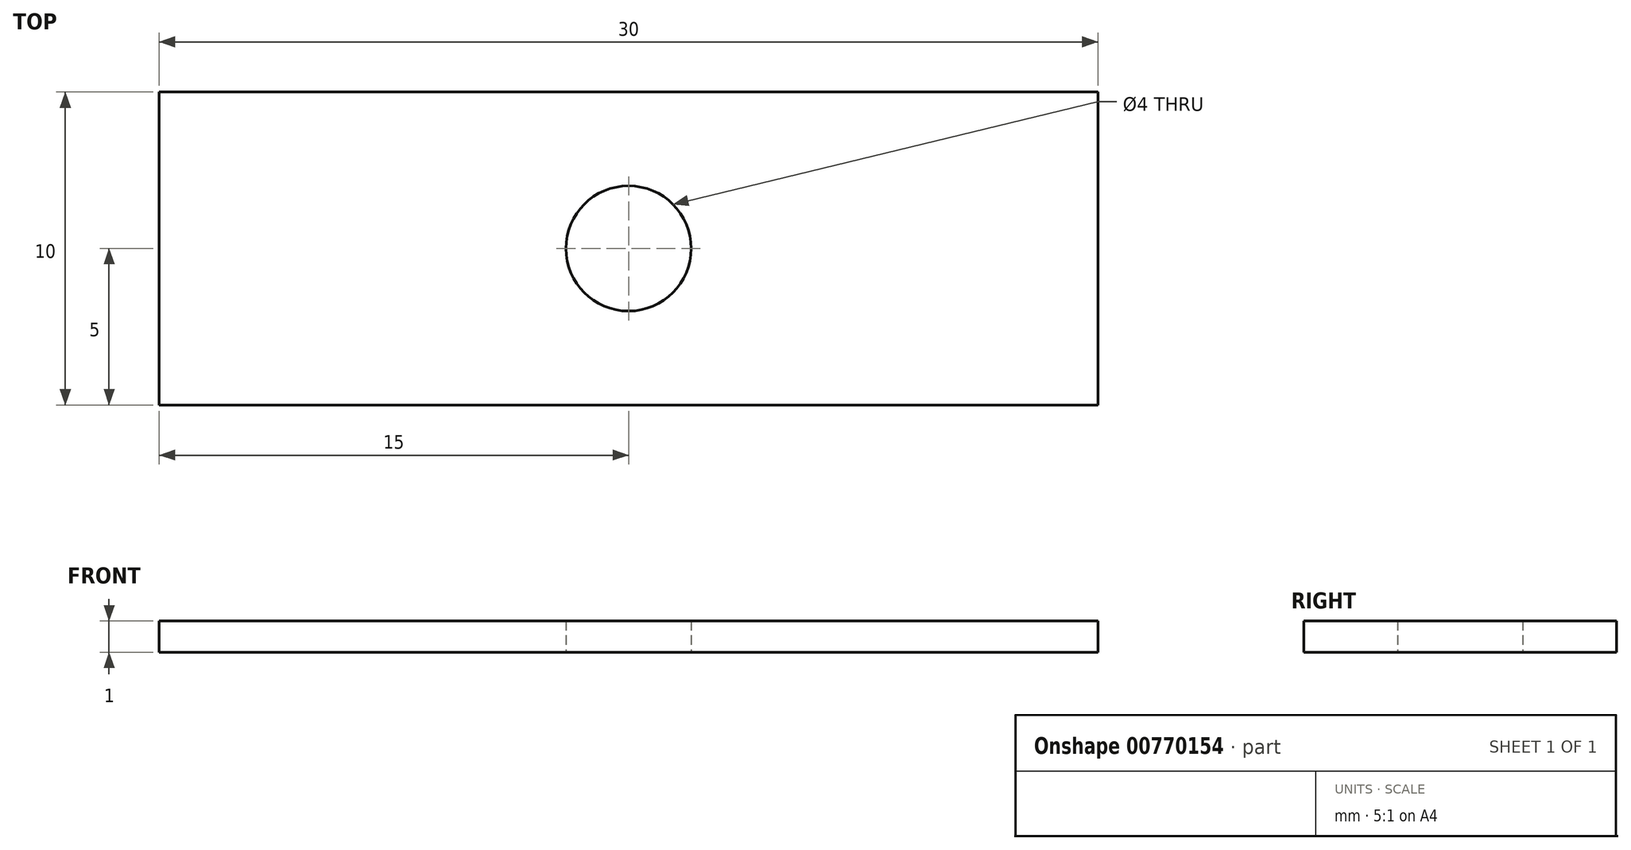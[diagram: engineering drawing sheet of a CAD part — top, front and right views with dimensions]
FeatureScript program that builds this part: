
annotation { "Feature Type Name" : "Feature", "Feature Type Description" : "" }
export const myFeature = defineFeature(function(context is Context, id is Id, definition is map)
    precondition{}
    {
        {
            var Q0;
            Q0=qCreatedBy(makeId("Top.planeOp"),FACE);
            var sketch = newSketch(context, id + "F0", { "sketchPlane" : qUnion([Q0])});
            skLineSegment(sketch, "E0.bottom", {"start": v(-15, 5) * mm, "end": v(15, 5) * mm});
            skLineSegment(sketch, "E0.top", {"start": v(-15, -5) * mm, "end": v(15, -5) * mm});
            skLineSegment(sketch, "E0.left", {"start": v(-15, 5) * mm, "end": v(-15, -5) * mm});
            skLineSegment(sketch, "E0.right", {"start": v(15, 5) * mm, "end": v(15, -5) * mm});
            skPoint(sketch, "E0.middle", {"position": v(0, 0) * mm});
            skCircle(sketch, "E1", {"center": v(0, 0) * mm, "radius": 2 * mm});
            skSolve(sketch);
        }
        {
            var Q0;
            Q0=qSketchRegion(id+"F0",true);
            extrude(context, id + "F1", {"entities" : qUnion([Q0]), "depth" : 1 * mm, "offsetDistance" : 25 * mm});
        }
    });
